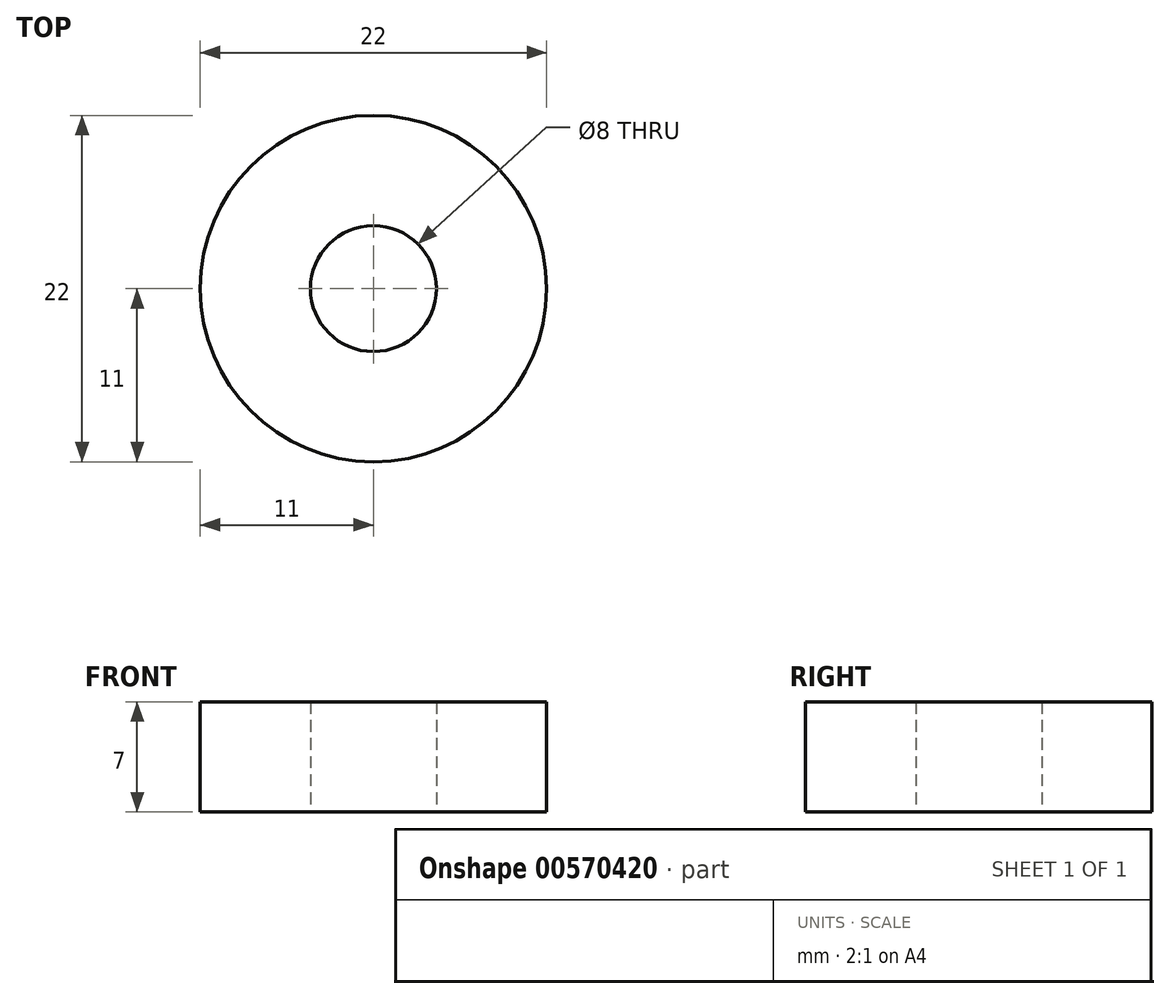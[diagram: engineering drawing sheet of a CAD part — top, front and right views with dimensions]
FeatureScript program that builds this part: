
annotation { "Feature Type Name" : "Feature", "Feature Type Description" : "" }
export const myFeature = defineFeature(function(context is Context, id is Id, definition is map)
    precondition{}
    {
        {
            var Q0;
            Q0=qCreatedBy(makeId("Top.planeOp"),FACE);
            var sketch = newSketch(context, id + "F0", { "sketchPlane" : qUnion([Q0])});
            skCircle(sketch, "E0", {"center": v(0, 0) * mm, "radius": 4 * mm});
            skCircle(sketch, "E1", {"center": v(0, 0) * mm, "radius": 11 * mm});
            skSolve(sketch);
        }
        {
            var Q0;
            Q0=makeQuery(id+"F0.imprint","IMPRINT",FACE,{"disambiguationData":[TD([[makeQuery(id+"F0.imprint","IMPRINT",EDGE,{"derivedFrom":sQuery(id+"F0.wireOp",EDGE,"E0")}),-1.0]])]});
            extrude(context, id + "F1", {"entities" : qUnion([Q0]), "depth" : 7 * mm, "offsetDistance" : 25 * mm});
        }
    });
